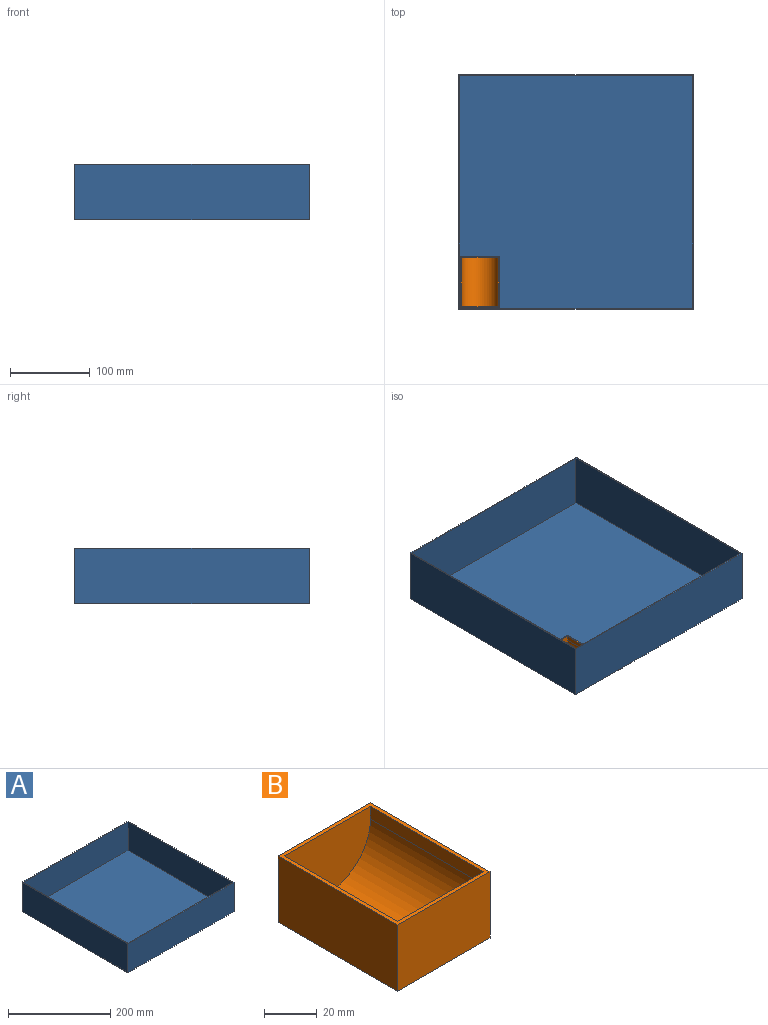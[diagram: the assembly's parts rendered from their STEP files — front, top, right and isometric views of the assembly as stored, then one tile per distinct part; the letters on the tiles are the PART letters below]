
ASSEMBLY  parts=2 mates=1
PART A: 11 faces, bbox 293.7x293.7x69.9 mm
  f0: plane 293.69x293.69mm, normal (0,0,-1), area 86252.3mm2, adj f5,f6,f7,f8
  f1: plane 290.51x68.26mm, normal (0,-1,0), area 19831.1mm2, adj f2,f4,f9,f10
  f2: plane 290.51x68.26mm, normal (1,0,0), area 19831.1mm2, adj f1,f3,f9,f10
  f3: plane 290.51x68.26mm, normal (0,1,0), area 19831.1mm2, adj f2,f4,f9,f10
  f4: plane 290.51x68.26mm, normal (-1,0,0), area 19831.1mm2, adj f1,f3,f9,f10
  f5: plane 293.69x69.85mm, normal (-1,0,0), area 20514.1mm2, adj f0,f6,f8,f9
  f6: plane 293.69x69.85mm, normal (0,1,0), area 20514.1mm2, adj f0,f5,f7,f9
  f7: plane 293.69x69.85mm, normal (1,0,0), area 20514.1mm2, adj f0,f6,f8,f9
  f8: plane 293.69x69.85mm, normal (0,-1,0), area 20514.1mm2, adj f0,f5,f7,f9
  f9: plane 293.69x293.69mm, normal (0,0,1), area 1854.8mm2, adj f1,f2,f3,f4,f5,f6,f7,f8
  f10: plane 290.51x290.51mm, normal (0,0,1), area 84397.5mm2, adj f1,f2,f3,f4
PART B: 11 faces, bbox 49.4x64x30.7 mm
  f0: plane 63.96x49.36mm, normal (0,0,1), area 369.5mm2, adj f2,f3,f4,f5,f6,f8,f9,f10
  f1: plane 63.96x49.36mm, normal (0,0,-1), area 3157.1mm2, adj f2,f3,f4,f5
  f2: plane 63.96x30.67mm, normal (1,0,0), area 1961.4mm2, adj f0,f1,f4,f5
  f3: plane 63.96x30.67mm, normal (-1,0,0), area 1961.4mm2, adj f0,f1,f4,f5
  f4: plane 49.36x30.67mm, normal (0,1,0), area 1513.7mm2, adj f0,f1,f2,f3
  f5: plane 49.36x30.67mm, normal (0,-1,0), area 1513.7mm2, adj f0,f1,f2,f3
  f6: plane 60.6x5.99mm, normal (1,0,0), area 362.8mm2, adj f0,f7,f9,f10
  f7: cylinder r=23mm len=60.6mm, axis (0,-1,0), area 4378.8mm2, adj f6,f8,f9,f10
  f8: plane 60.6x5.99mm, normal (-1,0,0), area 362.8mm2, adj f0,f7,f9,f10
  f9: plane 46x28.99mm, normal (0,-1,0), area 1106.3mm2, adj f0,f6,f7,f8
  f10: plane 46x28.99mm, normal (0,1,0), area 1106.3mm2, adj f0,f6,f7,f8
PLACE A rot(axis=(0,0,-1),90deg) t=(1.59,292.1,0)mm
PLACE B t=(26.83,3.97,26.27)mm
MATE planar B.f1 <-> A.f10  axis (0,0,-1) through (51.51,34.27,1.59)mm
